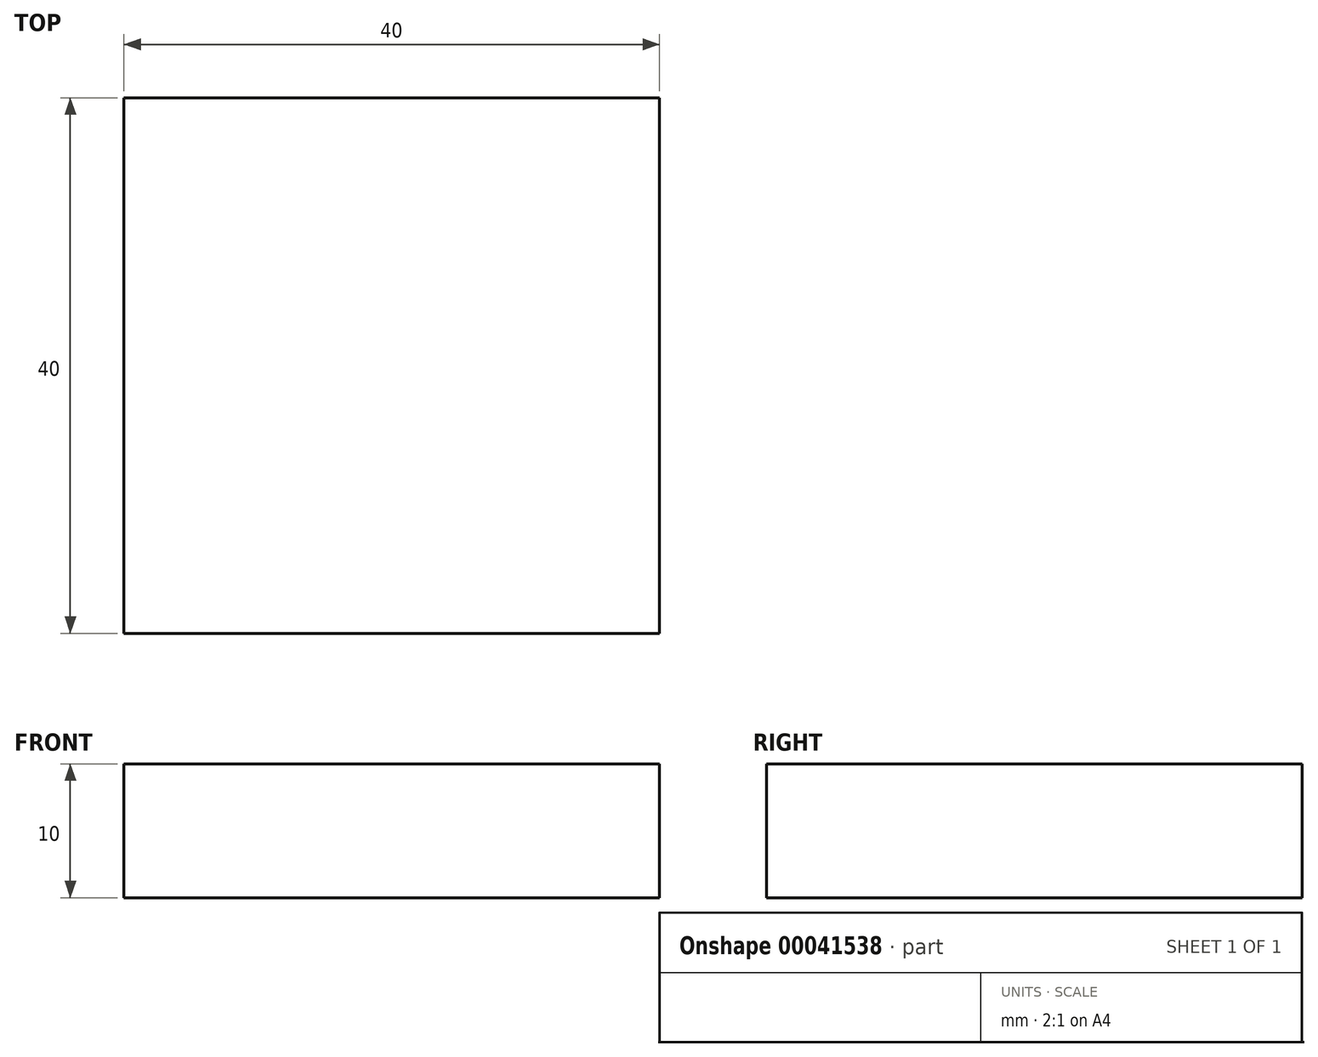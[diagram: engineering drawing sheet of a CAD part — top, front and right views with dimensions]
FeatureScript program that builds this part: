
annotation { "Feature Type Name" : "Feature", "Feature Type Description" : "" }
export const myFeature = defineFeature(function(context is Context, id is Id, definition is map)
    precondition{}
    {
        {
            var Q0;
            Q0=qCreatedBy(makeId("Top.planeOp"),FACE);
            var sketch = newSketch(context, id + "F0", { "sketchPlane" : qUnion([Q0])});
            skLineSegment(sketch, "E0.bottom", {"start": v(0, 0) * mm, "end": v(40, 0) * mm});
            skLineSegment(sketch, "E0.top", {"start": v(0, 40) * mm, "end": v(40, 40) * mm});
            skLineSegment(sketch, "E0.left", {"start": v(0, 0) * mm, "end": v(0, 40) * mm});
            skLineSegment(sketch, "E0.right", {"start": v(40, 0) * mm, "end": v(40, 40) * mm});
            skSolve(sketch);
        }
        {
            var Q0;
            Q0 = qSketchRegion(id + "F0", true);
            extrude(context, id + "F1", {"entities" : qUnion([Q0]), "depth" : 10 * mm});
        }
    });
